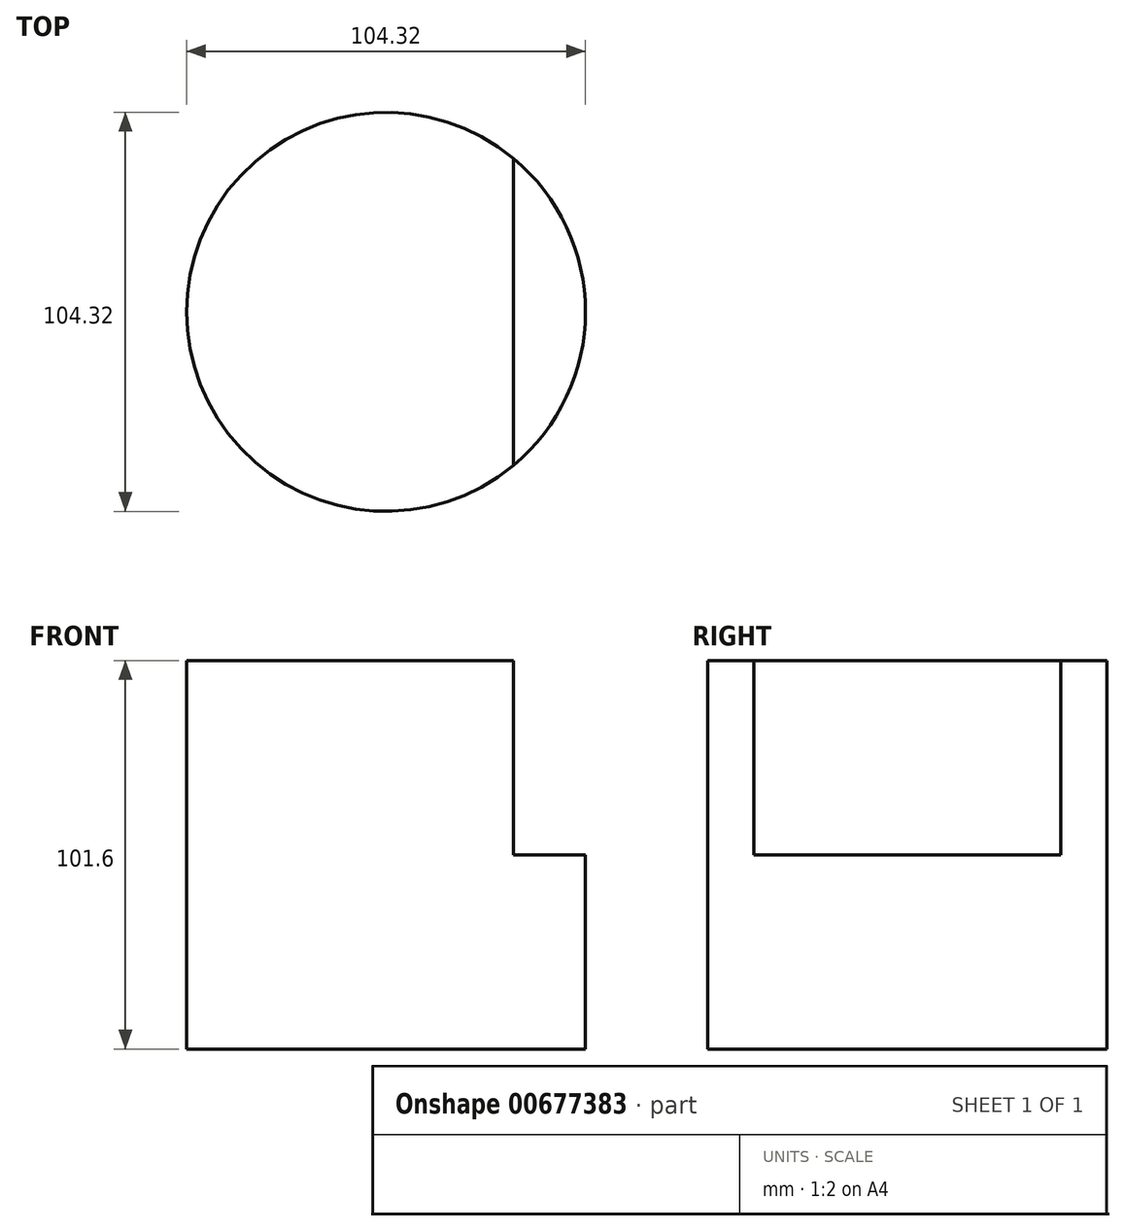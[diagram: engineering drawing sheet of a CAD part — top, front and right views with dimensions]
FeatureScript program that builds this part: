
annotation { "Feature Type Name" : "Feature", "Feature Type Description" : "" }
export const myFeature = defineFeature(function(context is Context, id is Id, definition is map)
    precondition{}
    {
        {
            var Q0;
            Q0=qCreatedBy(makeId("Top.planeOp"),FACE);
            var sketch = newSketch(context, id + "F0", { "sketchPlane" : qUnion([Q0])});
            skCircle(sketch, "E0", {"center": v(0, 0) * mm, "radius": 52.16 * mm});
            skSolve(sketch);
        }
        {
            var Q0;
            Q0 = qSketchRegion(id + "F0", true);
            extrude(context, id + "F1", {"entities" : qUnion([Q0]), "depth" : 101.6 * mm, "offsetDistance" : 25.4 * mm});
        }
        {
            var Q0;
            Q0=makeQuery(id+"F1.opExtrude","CAP_FACE",FACE,{"disambiguationData":[OSD([sQuery(id+"F0.wireOp",EDGE,"E0")])],"isStart":false});
            var sketch = newSketch(context, id + "F2", { "sketchPlane" : qUnion([Q0])});
            skLineSegment(sketch, "E1.bottom", {"start": v(33.31, 61.74) * mm, "end": v(101.8, 61.74) * mm});
            skLineSegment(sketch, "E1.top", {"start": v(33.31, -59.4) * mm, "end": v(101.8, -59.4) * mm});
            skLineSegment(sketch, "E1.left", {"start": v(33.31, 61.74) * mm, "end": v(33.31, -59.4) * mm});
            skLineSegment(sketch, "E1.right", {"start": v(101.8, 61.74) * mm, "end": v(101.8, -59.4) * mm});
            skSolve(sketch);
        }
        {
            var Q0;
            {var subQ4=sQuery(id+"F2.wireOp",EDGE,"E1.bottom");Q0=makeQuery(id+"F2.imprint","IMPRINT",FACE,{"disambiguationData":[TD([[makeQuery(id+"F2.imprint","IMPRINT",EDGE,{"derivedFrom":subQ4}),-1.0]])]});}
            var Q1;
            {var subQ0=sQuery(id+"F2.wireOp",EDGE,"E1.left");var subQ1=makeQuery(id+"F1.opExtrude","CAP_EDGE",EDGE,{"disambiguationData":[OSD([sQuery(id+"F0.wireOp",EDGE,"E0")])],"isStart":false});var subQ2=makeQuery(id+"F2.imprint","INTERSECT",VERTEX,{"disambiguationData":[OD(0.0)],"derivedFrom":[subQ1,subQ0]});Q1=makeQuery(id+"F2.imprint","IMPRINT",FACE,{"disambiguationData":[TD([[makeQuery(id+"F2.imprint","IMPRINT",EDGE,{"disambiguationData":[TD([[subQ2,-1.0]])],"derivedFrom":subQ0}),1.0]])]});}
            extrude(context, id + "F3", {"entities" : qUnion([Q0, Q1]), "operationType" : NewBodyOperationType.REMOVE, "oppositeDirection" : true, "depth" : 50.8 * mm, "offsetDistance" : 25.4 * mm});
        }
    });
